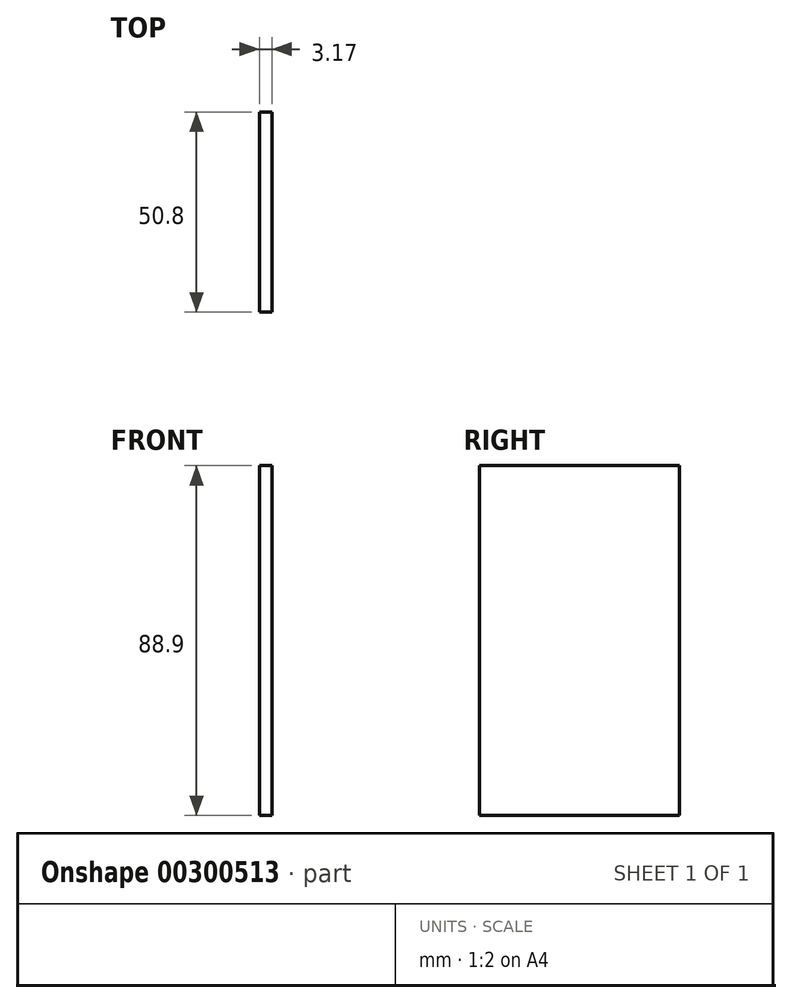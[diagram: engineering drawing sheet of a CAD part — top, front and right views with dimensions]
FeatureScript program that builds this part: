
annotation { "Feature Type Name" : "Feature", "Feature Type Description" : "" }
export const myFeature = defineFeature(function(context is Context, id is Id, definition is map)
    precondition{}
    {
        {
            var Q0;
            Q0=qCreatedBy(makeId("Right.planeOp"),FACE);
            var sketch = newSketch(context, id + "F0", { "sketchPlane" : qUnion([Q0])});
            skLineSegment(sketch, "E0.bottom", {"start": v(25.4, -44.45) * mm, "end": v(-25.4, -44.45) * mm});
            skLineSegment(sketch, "E0.top", {"start": v(25.4, 44.45) * mm, "end": v(-25.4, 44.45) * mm});
            skLineSegment(sketch, "E0.left", {"start": v(25.4, -44.45) * mm, "end": v(25.4, 44.45) * mm});
            skLineSegment(sketch, "E0.right", {"start": v(-25.4, -44.45) * mm, "end": v(-25.4, 44.45) * mm});
            skPoint(sketch, "E0.middle", {"position": v(0, 0) * mm});
            skSolve(sketch);
        }
        {
            var Q0;
            Q0 = qSketchRegion(id + "F0", true);
            extrude(context, id + "F1", {"entities" : qUnion([Q0]), "depth" : 3.17 * mm});
        }
    });
